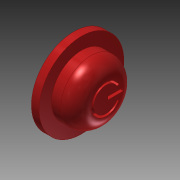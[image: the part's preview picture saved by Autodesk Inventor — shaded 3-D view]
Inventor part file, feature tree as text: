
AUTODESK INVENTOR PART (.ipt)
format: ipt  version: 2014 (Build 180170000, 170)  size: 137,216 bytes
history: native  units: mm
features: sketch x3, other x2, extrude x2, fillet x1
ambient origin geometry x8: Origin, YZ Plane, XZ Plane, XY Plane, X Axis, Y Axis, Z Axis, Center Point
bodies: Body1 (feature_tree)
feature tree (8):
  other  "Твердое тело1"
  extrude  "Выдавливание1"  Depth=11.0mm
  extrude  "Выдавливание2"  Depth=1.0mm TaperAngle=0.0deg
  fillet  "Сопряжение1"  Radius=7.8mm
  other  "Рельеф1"
  sketch  "Эскиз1"
  sketch  "Эскиз2"
  sketch  "Эскиз3"
